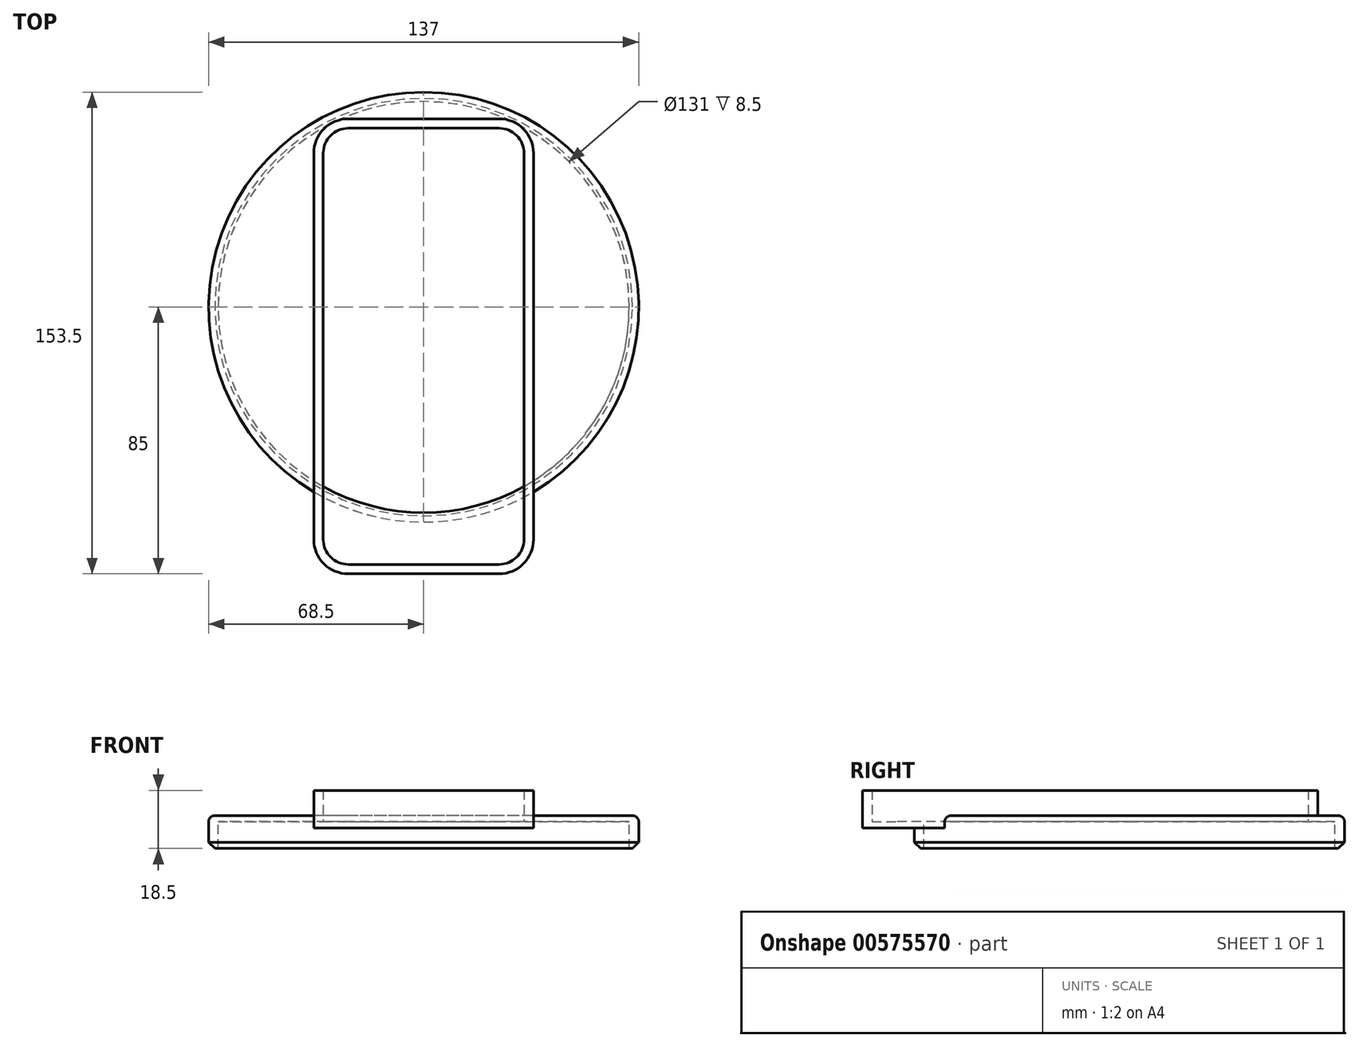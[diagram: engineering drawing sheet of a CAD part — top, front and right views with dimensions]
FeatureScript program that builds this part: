
annotation { "Feature Type Name" : "Feature", "Feature Type Description" : "" }
export const myFeature = defineFeature(function(context is Context, id is Id, definition is map)
    precondition{}
    {
        {
            var Q0;
            Q0=qCreatedBy(makeId("Top.planeOp"),FACE);
            var sketch = newSketch(context, id + "F0", { "sketchPlane" : qUnion([Q0])});
            skCircle(sketch, "E0", {"center": v(0, 0) * mm, "radius": 65.5 * mm});
            skCircle(sketch, "E1.0", {"center": v(0, 0) * mm, "radius": 68.5 * mm});
            skSolve(sketch);
        }
        {
            var Q0;
            Q0 = qSketchRegion(id + "F0", true);
            var Q1;
            Q1=makeQuery(id+"F0.imprint","IMPRINT",FACE,{"disambiguationData":[TD([[makeQuery(id+"F0.imprint","IMPRINT",EDGE,{"derivedFrom":sQuery(id+"F0.wireOp",EDGE,"E0")}),1.0]])]});
            extrude(context, id + "F1", {"entities" : qUnion([Q0, Q1]), "depth" : 2 * mm, "offsetDistance" : 25 * mm});
        }
        {
            var Q0;
            Q0 = qSketchRegion(id + "F0", true);
            extrude(context, id + "F2", {"entities" : qUnion([Q0]), "operationType" : NewBodyOperationType.ADD, "oppositeDirection" : true, "depth" : 8.5 * mm, "offsetDistance" : 25 * mm});
        }
        {
            var Q0;
            Q0=makeQuery(id+"F2.opExtrude","CAP_EDGE",EDGE,{"disambiguationData":[OSD([sQuery(id+"F0.wireOp",EDGE,"E1.0")])],"isStart":false});
            chamfer(context, id + "F3", {"entities" : qUnion([Q0]), "width" : 2 * mm, "tangentPropagation" : true});
        }
        {
            var Q0;
            Q0=qCreatedBy(makeId("Top.planeOp"),FACE);
            var sketch = newSketch(context, id + "F4", { "sketchPlane" : qUnion([Q0])});
            skLineSegment(sketch, "E2.bottom", {"start": v(-24, 57) * mm, "end": v(24, 57) * mm});
            skLineSegment(sketch, "E2.top", {"start": v(-24, -82) * mm, "end": v(24, -82) * mm});
            skLineSegment(sketch, "E2.left", {"start": v(-32, 49) * mm, "end": v(-32, -74) * mm});
            skLineSegment(sketch, "E2.right", {"start": v(32, 49) * mm, "end": v(32, -74) * mm});
            skLineSegment(sketch, "E3", {"start": v(0, 57) * mm, "end": v(0, 0) * mm});
            skPoint(sketch, "E4.visualSharp", {"position": v(-32, 57) * mm});
            skArc(sketch, "E4.filletArc", {"start": v(-24, 57) * mm, "mid": v(-29.66, 54.66) * mm, "end": v(-32, 49) * mm});
            skPoint(sketch, "E5.visualSharp", {"position": v(32, 57) * mm});
            skArc(sketch, "E5.filletArc", {"start": v(32, 49) * mm, "mid": v(29.66, 54.66) * mm, "end": v(24, 57) * mm});
            skPoint(sketch, "E6.visualSharp", {"position": v(32, -82) * mm});
            skArc(sketch, "E6.filletArc", {"start": v(24, -82) * mm, "mid": v(29.66, -79.66) * mm, "end": v(32, -74) * mm});
            skPoint(sketch, "E7.visualSharp", {"position": v(-32, -82) * mm});
            skArc(sketch, "E7.filletArc", {"start": v(-32, -74) * mm, "mid": v(-29.66, -79.66) * mm, "end": v(-24, -82) * mm});
            skArc(sketch, "E8.0", {"start": v(35, 49) * mm, "mid": v(31.78, 56.78) * mm, "end": v(24, 60) * mm});
            skLineSegment(sketch, "E8.1", {"start": v(-24, 60) * mm, "end": v(24, 60) * mm});
            skLineSegment(sketch, "E8.2", {"start": v(35, 49) * mm, "end": v(35, -74) * mm});
            skArc(sketch, "E8.3", {"start": v(-24, 60) * mm, "mid": v(-31.78, 56.78) * mm, "end": v(-35, 49) * mm});
            skArc(sketch, "E8.4", {"start": v(24, -85) * mm, "mid": v(31.78, -81.78) * mm, "end": v(35, -74) * mm});
            skLineSegment(sketch, "E8.5", {"start": v(-24, -85) * mm, "end": v(24, -85) * mm});
            skArc(sketch, "E8.6", {"start": v(-35, -74) * mm, "mid": v(-31.78, -81.78) * mm, "end": v(-24, -85) * mm});
            skLineSegment(sketch, "E8.7", {"start": v(-35, 49) * mm, "end": v(-35, -74) * mm});
            skSolve(sketch);
        }
        {
            var Q0;
            Q0=makeQuery(id+"F4.imprint","IMPRINT",FACE,{"disambiguationData":[TD([[makeQuery(id+"F4.imprint","IMPRINT",EDGE,{"derivedFrom":sQuery(id+"F4.wireOp",EDGE,"E2.top")}),1.0]])]});
            var Q1;
            Q1=makeQuery(id+"F4.imprint","IMPRINT",FACE,{"disambiguationData":[TD([[makeQuery(id+"F4.imprint","IMPRINT",EDGE,{"derivedFrom":sQuery(id+"F4.wireOp",EDGE,"E2.top")}),-1.0]])]});
            var Q2;
            Q2 = qSketchRegion(id + "F4", true);
            extrude(context, id + "F5", {"entities" : qUnion([Q0, Q1, Q2]), "operationType" : NewBodyOperationType.ADD, "oppositeDirection" : true, "depth" : 2 * mm, "offsetDistance" : 25 * mm});
        }
        {
            var Q0;
            Q0=makeQuery(id+"F4.imprint","IMPRINT",FACE,{"disambiguationData":[TD([[makeQuery(id+"F4.imprint","IMPRINT",EDGE,{"derivedFrom":sQuery(id+"F4.wireOp",EDGE,"E2.top")}),1.0]])]});
            extrude(context, id + "F6", {"entities" : qUnion([Q0]), "operationType" : NewBodyOperationType.REMOVE, "depth" : 3 * mm, "offsetDistance" : 25 * mm});
        }
        {
            var Q0;
            Q0=makeQuery(id+"F4.imprint","IMPRINT",FACE,{"disambiguationData":[TD([[makeQuery(id+"F4.imprint","IMPRINT",EDGE,{"derivedFrom":sQuery(id+"F4.wireOp",EDGE,"E2.top")}),-1.0]])]});
            extrude(context, id + "F7", {"entities" : qUnion([Q0]), "operationType" : NewBodyOperationType.ADD, "depth" : 10 * mm, "offsetDistance" : 25 * mm});
        }
        {
            var Q0;
            Q0=makeQuery(id+"F0.imprint","IMPRINT",FACE,{"disambiguationData":[TD([[makeQuery(id+"F0.imprint","IMPRINT",EDGE,{"derivedFrom":sQuery(id+"F0.wireOp",EDGE,"E0")}),1.0]])]});
            extrude(context, id + "F8", {"entities" : qUnion([Q0]), "operationType" : NewBodyOperationType.REMOVE, "oppositeDirection" : true, "depth" : 25 * mm, "offsetDistance" : 25 * mm});
        }
        {
            var Q0;
            Q0=makeQuery(id+"F1.opExtrude","CAP_EDGE",EDGE,{"disambiguationData":[OSD([sQuery(id+"F0.wireOp",EDGE,"E1.0")])],"isStart":false});
            fillet(context, id + "F9", {"entities" : qUnion([Q0]), "radius" : 2 * mm, "tangentPropagation" : true, "allowEdgeOverflow" : false});
        }
    });
